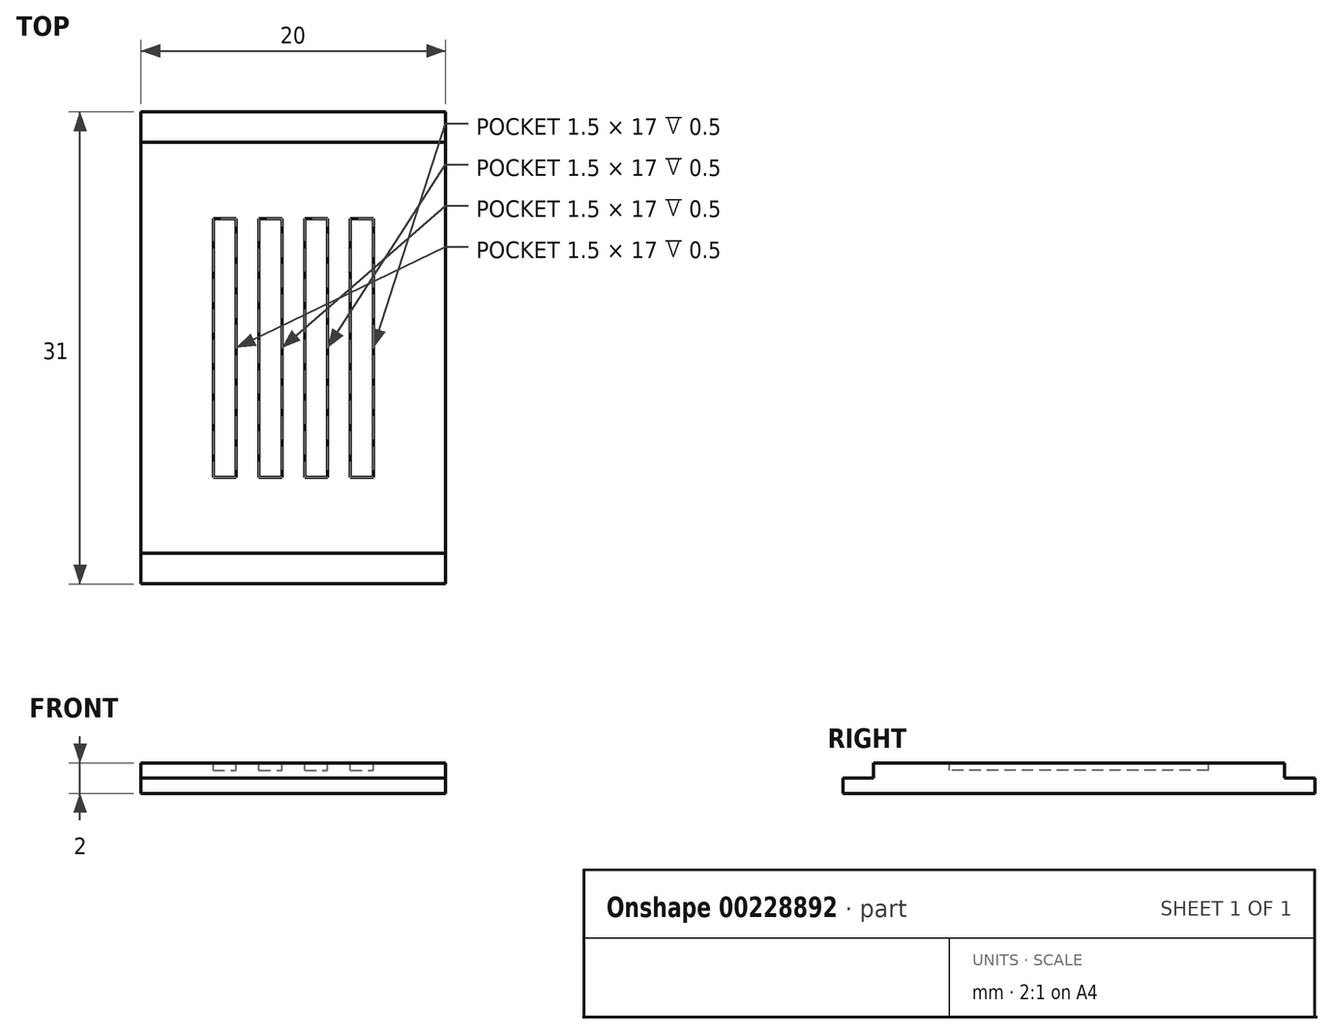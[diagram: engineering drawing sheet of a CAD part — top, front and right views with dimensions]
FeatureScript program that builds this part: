
annotation { "Feature Type Name" : "Feature", "Feature Type Description" : "" }
export const myFeature = defineFeature(function(context is Context, id is Id, definition is map)
    precondition{}
    {
        {
            var Q0;
            Q0=qCreatedBy(makeId("Top.planeOp"),FACE);
            var sketch = newSketch(context, id + "F0", { "sketchPlane" : qUnion([Q0])});
            skLineSegment(sketch, "E0.bottom", {"start": v(-2.97, 16.32) * mm, "end": v(17.03, 16.32) * mm});
            skLineSegment(sketch, "E0.top", {"start": v(-2.97, -14.68) * mm, "end": v(17.03, -14.68) * mm});
            skLineSegment(sketch, "E0.left", {"start": v(-2.97, 16.32) * mm, "end": v(-2.97, -14.68) * mm});
            skLineSegment(sketch, "E0.right", {"start": v(17.03, 16.32) * mm, "end": v(17.03, -14.68) * mm});
            skSolve(sketch);
        }
        {
            var Q0;
            Q0 = qSketchRegion(id + "F0", true);
            extrude(context, id + "F1", {"entities" : qUnion([Q0]), "depth" : 1 * mm, "offsetDistance" : 25 * mm});
        }
        {
            var Q0;
            Q0=makeQuery(id+"F1.opExtrude","CAP_FACE",FACE,{"disambiguationData":[OSD([sQuery(id+"F0.wireOp",EDGE,"E0.bottom"),sQuery(id+"F0.wireOp",EDGE,"E0.top"),sQuery(id+"F0.wireOp",EDGE,"E0.left"),sQuery(id+"F0.wireOp",EDGE,"E0.right")])],"isStart":false});
            var sketch = newSketch(context, id + "F2", { "sketchPlane" : qUnion([Q0])});
            skLineSegment(sketch, "E1.bottom", {"start": v(-2.97, 14.32) * mm, "end": v(17.03, 14.32) * mm});
            skLineSegment(sketch, "E1.top", {"start": v(-2.97, -12.68) * mm, "end": v(17.03, -12.68) * mm});
            skLineSegment(sketch, "E1.left", {"start": v(-2.97, 14.32) * mm, "end": v(-2.97, -12.68) * mm});
            skLineSegment(sketch, "E1.right", {"start": v(17.03, 14.32) * mm, "end": v(17.03, -12.68) * mm});
            skSolve(sketch);
        }
        {
            var Q0;
            Q0 = qSketchRegion(id + "F2", true);
            extrude(context, id + "F3", {"entities" : qUnion([Q0]), "operationType" : NewBodyOperationType.ADD, "depth" : 1 * mm, "offsetDistance" : 25 * mm});
        }
        {
            var Q0;
            Q0=makeQuery(id+"F3.opExtrude","CAP_FACE",FACE,{"disambiguationData":[OSD([sQuery(id+"F2.wireOp",EDGE,"E1.bottom"),sQuery(id+"F2.wireOp",EDGE,"E1.top"),sQuery(id+"F2.wireOp",EDGE,"E1.left"),sQuery(id+"F2.wireOp",EDGE,"E1.right")])],"isStart":false});
            var sketch = newSketch(context, id + "F4", { "sketchPlane" : qUnion([Q0])});
            skLineSegment(sketch, "E2.bottom", {"start": v(1.78, 9.32) * mm, "end": v(3.28, 9.32) * mm});
            skLineSegment(sketch, "E2.top", {"start": v(1.78, -7.68) * mm, "end": v(3.28, -7.68) * mm});
            skLineSegment(sketch, "E2.left", {"start": v(1.78, 9.32) * mm, "end": v(1.78, -7.68) * mm});
            skLineSegment(sketch, "E2.right", {"start": v(3.28, 9.32) * mm, "end": v(3.28, -7.68) * mm});
            skLineSegment(sketch, "E3.1.0.0", {"start": v(4.78, 9.32) * mm, "end": v(4.78, -7.68) * mm});
            skLineSegment(sketch, "E3.1.0.1", {"start": v(6.28, 9.32) * mm, "end": v(6.28, -7.68) * mm});
            skLineSegment(sketch, "E3.1.0.2", {"start": v(4.78, -7.68) * mm, "end": v(6.28, -7.68) * mm});
            skLineSegment(sketch, "E3.1.0.3", {"start": v(4.78, 9.32) * mm, "end": v(6.28, 9.32) * mm});
            skLineSegment(sketch, "E3.2.0.0", {"start": v(7.78, 9.32) * mm, "end": v(7.78, -7.68) * mm});
            skLineSegment(sketch, "E3.2.0.1", {"start": v(9.28, 9.32) * mm, "end": v(9.28, -7.68) * mm});
            skLineSegment(sketch, "E3.2.0.2", {"start": v(7.78, -7.68) * mm, "end": v(9.28, -7.68) * mm});
            skLineSegment(sketch, "E3.2.0.3", {"start": v(7.78, 9.32) * mm, "end": v(9.28, 9.32) * mm});
            skLineSegment(sketch, "E3.3.0.0", {"start": v(10.78, 9.32) * mm, "end": v(10.78, -7.68) * mm});
            skLineSegment(sketch, "E3.3.0.1", {"start": v(12.28, 9.32) * mm, "end": v(12.28, -7.68) * mm});
            skLineSegment(sketch, "E3.3.0.2", {"start": v(10.78, -7.68) * mm, "end": v(12.28, -7.68) * mm});
            skLineSegment(sketch, "E3.3.0.3", {"start": v(10.78, 9.32) * mm, "end": v(12.28, 9.32) * mm});
            skLineSegment(sketch, "E3.direction1", {"start": v(1.78, -7.68) * mm, "end": v(4.78, -7.68) * mm, "construction": true});
            skSolve(sketch);
        }
        {
            var Q0;
            Q0 = qSketchRegion(id + "F4", true);
            extrude(context, id + "F5", {"entities" : qUnion([Q0]), "operationType" : NewBodyOperationType.REMOVE, "oppositeDirection" : true, "depth" : 0.5 * mm, "offsetDistance" : 25 * mm});
        }
    });
